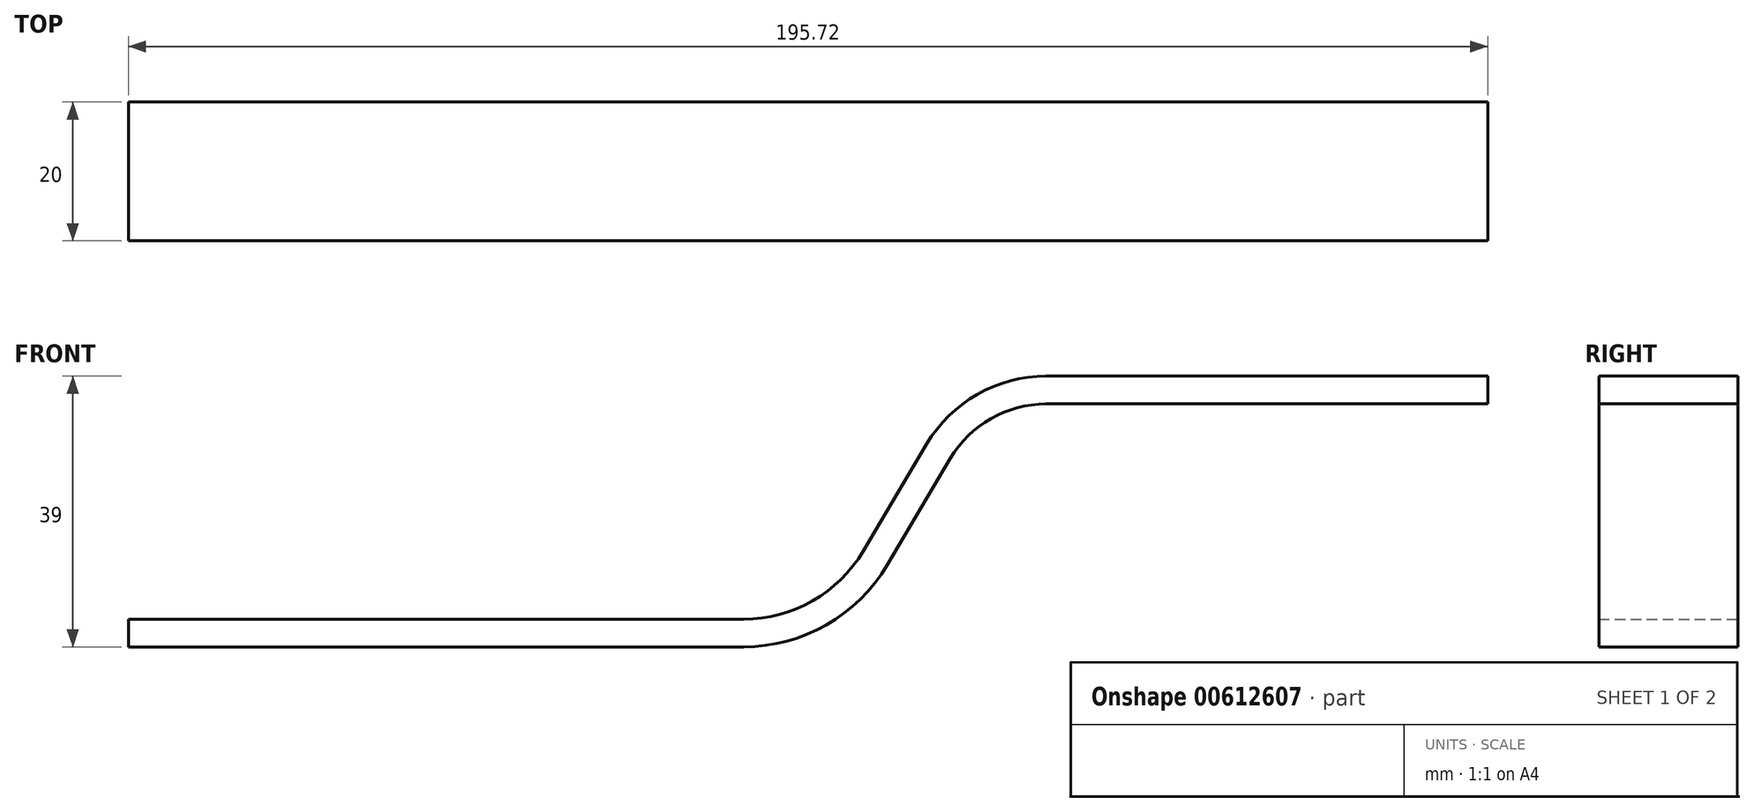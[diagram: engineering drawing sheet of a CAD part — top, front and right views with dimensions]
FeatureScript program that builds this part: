
annotation { "Feature Type Name" : "Feature", "Feature Type Description" : "" }
export const myFeature = defineFeature(function(context is Context, id is Id, definition is map)
    precondition{}
    {
        {
            var Q0;
            Q0=qCreatedBy(makeId("Front.planeOp"),FACE);
            var sketch = newSketch(context, id + "F0", { "sketchPlane" : qUnion([Q0])});
            skLineSegment(sketch, "E0", {"start": v(-133.32, 0) * mm, "end": v(-44.72, 0) * mm});
            skLineSegment(sketch, "E1", {"start": v(-27.51, 9.81) * mm, "end": v(-18.4, 25.19) * mm});
            skLineSegment(sketch, "E2", {"start": v(-1.2, 35) * mm, "end": v(62.4, 35) * mm});
            skPoint(sketch, "E3.visualSharp", {"position": v(-33.32, 0) * mm});
            skArc(sketch, "E3.filletArc", {"start": v(-44.72, 0) * mm, "mid": v(-34.82, 2.62) * mm, "end": v(-27.51, 9.81) * mm});
            skPoint(sketch, "E4.visualSharp", {"position": v(-12.6, 35) * mm});
            skArc(sketch, "E4.filletArc", {"start": v(-1.2, 35) * mm, "mid": v(-11.1, 32.38) * mm, "end": v(-18.4, 25.19) * mm});
            skLineSegment(sketch, "E5.0", {"start": v(-1.2, 31) * mm, "end": v(62.4, 31) * mm});
            skLineSegment(sketch, "E5.1", {"start": v(-133.32, -4) * mm, "end": v(-44.72, -4) * mm});
            skArc(sketch, "E5.2", {"start": v(-44.72, -4) * mm, "mid": v(-32.84, -0.85) * mm, "end": v(-24.07, 7.77) * mm});
            skLineSegment(sketch, "E5.3", {"start": v(-24.07, 7.77) * mm, "end": v(-14.96, 23.15) * mm});
            skArc(sketch, "E5.4", {"start": v(-1.2, 31) * mm, "mid": v(-9.12, 28.9) * mm, "end": v(-14.96, 23.15) * mm});
            skLineSegment(sketch, "E6", {"start": v(-133.32, 0) * mm, "end": v(-133.32, -4) * mm});
            skLineSegment(sketch, "E7", {"start": v(62.4, 35) * mm, "end": v(62.4, 31) * mm});
            skSolve(sketch);
        }
        {
            var Q0;
            Q0=makeQuery(id+"F0.imprint","IMPRINT",FACE,{"disambiguationData":[TD([[makeQuery(id+"F0.imprint","IMPRINT",EDGE,{"derivedFrom":sQuery(id+"F0.wireOp",EDGE,"E0")}),-1.0]])]});
            extrude(context, id + "F1", {"entities" : qUnion([Q0]), "depth" : 20 * mm, "offsetDistance" : 25.4 * mm});
        }
    });
